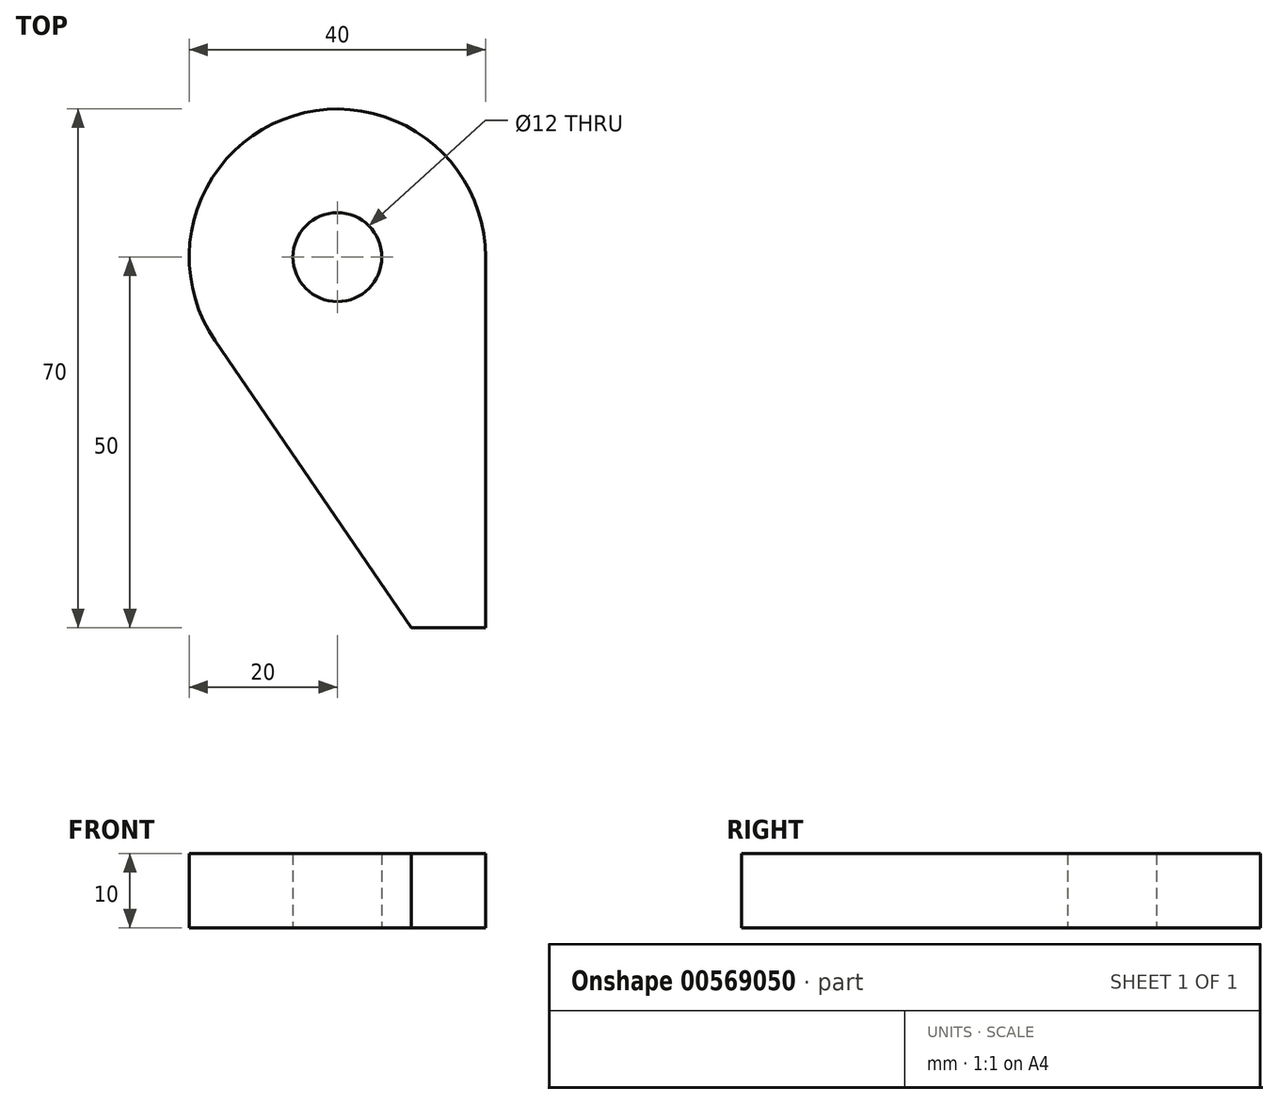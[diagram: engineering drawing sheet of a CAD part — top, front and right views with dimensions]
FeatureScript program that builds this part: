
annotation { "Feature Type Name" : "Feature", "Feature Type Description" : "" }
export const myFeature = defineFeature(function(context is Context, id is Id, definition is map)
    precondition{}
    {
        {
            var Q0;
            Q0=qCreatedBy(makeId("Top.planeOp"), FACE);
            var sketch = newSketch(context, id + "F0", { "sketchPlane" : qUnion([Q0])});
            skCircle(sketch, "E0", {"center": v(0, 0) * mm, "radius": 6 * mm});
            skArc(sketch, "E1", {"start": v(20, 0) * mm, "mid": v(-5.91, 19.1) * mm, "end": v(-16.5, -11.3) * mm});
            skLineSegment(sketch, "E2", {"start": v(20, 0) * mm, "end": v(20, -50) * mm});
            skLineSegment(sketch, "E3", {"start": v(20, -50) * mm, "end": v(10, -50) * mm});
            skLineSegment(sketch, "E4", {"start": v(10, -50) * mm, "end": v(-16.5, -11.3) * mm});
            skSolve(sketch);
        }
        {
            var Q0;
            Q0 = qSketchRegion(id + "F0", true);
            extrude(context, id + "F1", {"entities" : qUnion([Q0]), "depth" : 10 * mm, "offsetDistance" : 25 * mm});
        }
    });
